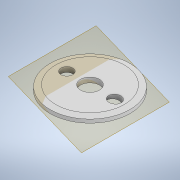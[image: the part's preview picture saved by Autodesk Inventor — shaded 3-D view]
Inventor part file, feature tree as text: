
AUTODESK INVENTOR PART (.ipt)
format: ipt  version: 2021 (Build 250183000, 183)  size: 173,056 bytes
history: native  units: mm
features: sketch x5, extrude x4, revolve x1, plane x1
ambient origin geometry x8: Origin, YZ Plane, XZ Plane, XY Plane, X Axis, Y Axis, Z Axis, Center Point
bodies: Solid1 (feature_tree)
feature tree (11):
  revolve  "Revolution1"  [1 undecoded]
  extrude  "Extrusion1"  Depth=3.5mm
  plane  "Work Plane1"
  extrude  "Extrusion2"  Depth=73.5mm
  extrude  "Extrusion3"  TaperAngle=90.0deg  [1 undecoded]
  extrude  "Extrusion4"  TaperAngle=0.0deg  [1 undecoded]
  sketch  "Sketch1"  dims[d0=95.0mm d1=12.0mm]
  sketch  "Sketch2"  dims[d2=8.4mm d3=3.5mm]
  sketch  "Sketch3"  dims[d4=3.0mm d5=73.5mm]
  sketch  "Sketch4"  dims[d6=165.0deg d7=90.0deg]
  sketch  "Sketch5"  dims[d8=45.0mm d9=0.0mm d10=0.0mm d11=11.868239mm d12=5.0mm d13=54.5mm d14=28.0mm d15=73.0mm d16=0.0mm d17=97.5mm d18=10.0mm d19=0.5mm d20=0.0mm d21=28.0mm d22=55.0mm d23=0.0mm d24=0.0mm]
note: 3 required parameter values undecoded (feature->parameter linkage not recoverable at this tier; creation-order binding heuristic only, values carry confidence <= 0.55)